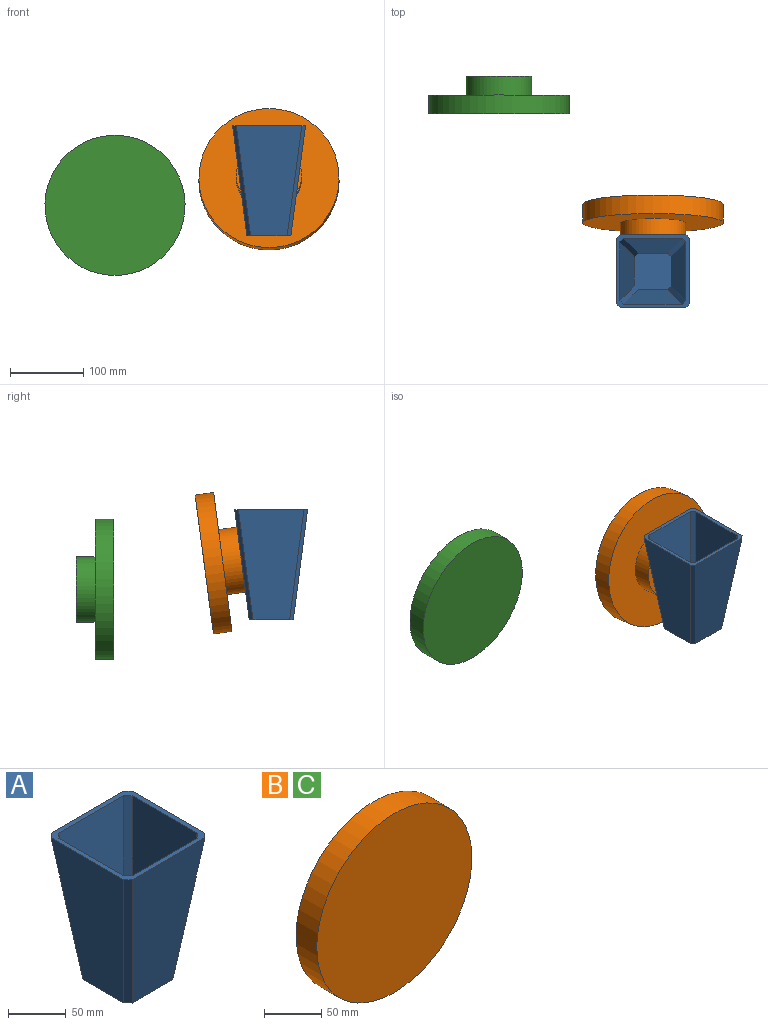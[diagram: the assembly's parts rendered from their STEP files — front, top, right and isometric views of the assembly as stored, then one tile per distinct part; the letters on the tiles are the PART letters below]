
ASSEMBLY  parts=3 mates=1
PART A: 19 faces, bbox 99.4x99.4x150 mm
  f0: plane 60x60mm, normal (0,0,-1), area 3549.2mm2, adj f2,f3,f4,f5,f15,f16,f17,f18
  f1: plane 99.35x99.35mm, normal (0,0,1), area 1771.2mm2, adj f2,f3,f4,f5,f7,f8,f9,f10
  f2: plane 150x89.27mm, normal (-0.99,0,-0.13), area 10525.6mm2, adj f0,f1,f17,f18
  f3: plane 150x89.27mm, normal (0,-0.99,-0.13), area 10526.9mm2, adj f0,f1,f16,f18
  f4: plane 150x89.28mm, normal (0.99,0,-0.13), area 10532.3mm2, adj f0,f1,f15,f16
  f5: plane 150x89.27mm, normal (0,0.99,-0.13), area 10531mm2, adj f0,f1,f15,f17
  f6: plane 50x50mm, normal (0,0,1), area 2449mm2, adj f7,f8,f9,f10,f11,f12,f13,f14
  f7: plane 140x79.9mm, normal (0,0.99,0.14), area 8471.2mm2, adj f1,f6,f11,f12
  f8: plane 140x79.9mm, normal (-0.99,0,0.14), area 8471.2mm2, adj f1,f6,f11,f13
  f9: plane 140x79.9mm, normal (0,-0.99,0.14), area 8471.2mm2, adj f1,f6,f13,f14
  f10: plane 140x79.9mm, normal (0.99,0,0.14), area 8471.2mm2, adj f1,f6,f12,f14
  f11: plane 140x25.05mm, normal (-0.69,0.69,0.2), area 1020mm2, adj f1,f6,f7,f8
  f12: plane 140x25.05mm, normal (0.69,0.69,0.2), area 1020mm2, adj f1,f6,f7,f10
  f13: plane 140x25.05mm, normal (-0.69,-0.69,0.2), area 1020mm2, adj f1,f6,f8,f9
  f14: plane 140x25.05mm, normal (0.69,-0.69,0.2), area 1020mm2, adj f1,f6,f9,f10
  f15: plane 150x25.04mm, normal (0.69,0.69,-0.18), area 1087.6mm2, adj f0,f1,f4,f5
  f16: plane 150x25.04mm, normal (0.7,-0.7,-0.18), area 1087.4mm2, adj f0,f1,f3,f4
  f17: plane 150x24.91mm, normal (-0.7,0.7,-0.18), area 1087.3mm2, adj f0,f1,f2,f5
  f18: plane 150x24.52mm, normal (-0.7,-0.7,-0.18), area 1087.1mm2, adj f0,f1,f2,f3
PART B: 5 faces, bbox 190.8x50.8x190.8 mm
  f0: cylinder r=95.42mm len=190.83mm, axis (0,1,0), area 15227.7mm2, adj f1,f2
  f1: plane 190.83x190.83mm, normal (0,-1,0), area 28601.6mm2, adj f0
  f2: plane 190.83x190.83mm, normal (0,1,0), area 22348mm2, adj f0,f3
  f3: cylinder r=44.62mm len=89.23mm, axis (0,-1,0), area 7120.4mm2, adj f2,f4
  f4: plane 89.23x89.23mm, normal (0,1,0), area 6253.5mm2, adj f3
PART C: same geometry as B
PLACE A t=(94.84,-98.45,30.94)mm
PLACE B rot(axis=(1,0,0),172.5deg) t=(108.84,-27.16,79.19)mm fixed
PLACE C t=(-100.8,141.54,-37.33)mm
MATE revolute B.f0 <-> A.f5  axis (0,-0.99,0.13) through (95.02,-57.58,43)mm
